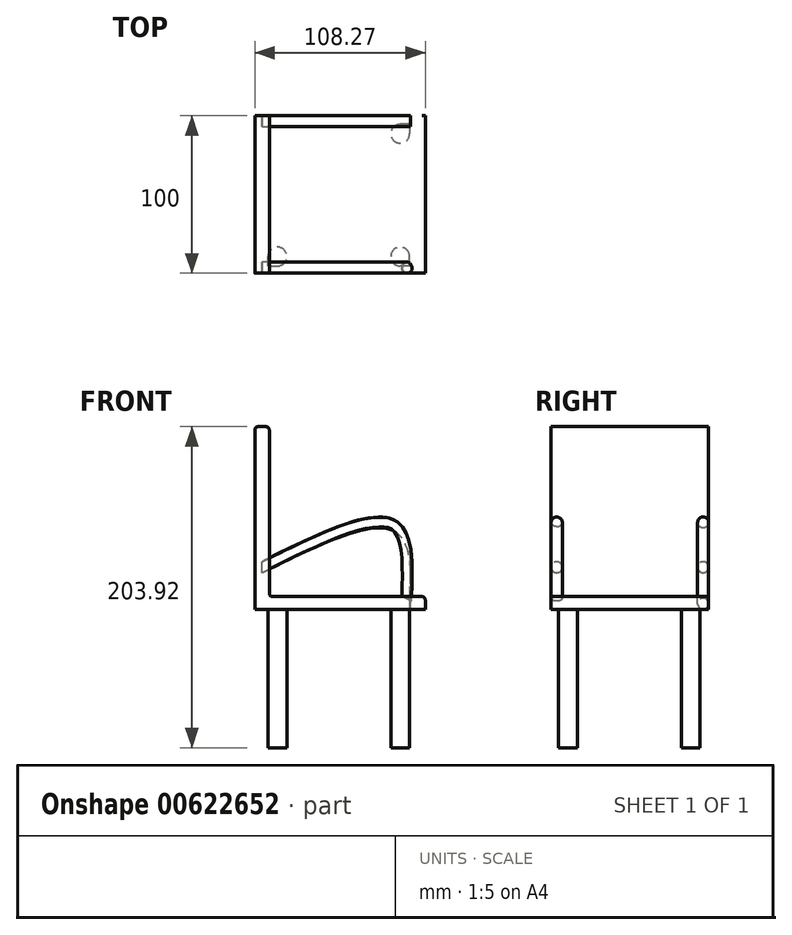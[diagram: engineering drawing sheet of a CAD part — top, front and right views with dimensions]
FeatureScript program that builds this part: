
annotation { "Feature Type Name" : "Feature", "Feature Type Description" : "" }
export const myFeature = defineFeature(function(context is Context, id is Id, definition is map)
    precondition{}
    {
        {
            var Q0;
            Q0=qCreatedBy(makeId("Front.planeOp"),FACE);
            var sketch = newSketch(context, id + "F0", { "sketchPlane" : qUnion([Q0])});
            skLineSegment(sketch, "E0.bottom", {"start": v(-52.86, 60.82) * mm, "end": v(-47.66, 60.82) * mm});
            skLineSegment(sketch, "E0.top", {"start": v(-54.86, -55.1) * mm, "end": v(-45.66, -55.1) * mm});
            skLineSegment(sketch, "E0.left", {"start": v(-54.86, 58.82) * mm, "end": v(-54.86, -55.1) * mm});
            skLineSegment(sketch, "E0.right", {"start": v(-45.66, 58.82) * mm, "end": v(-45.66, -45.1) * mm});
            skLineSegment(sketch, "E1.bottom", {"start": v(-43.66, -47.1) * mm, "end": v(51.4, -47.1) * mm});
            skLineSegment(sketch, "E1.top", {"start": v(-54.86, -55.1) * mm, "end": v(53.4, -55.1) * mm});
            skLineSegment(sketch, "E1.left", {"start": v(-54.86, -47.1) * mm, "end": v(-54.86, -55.1) * mm});
            skLineSegment(sketch, "E1.right", {"start": v(53.4, -49.1) * mm, "end": v(53.4, -55.1) * mm});
            skPoint(sketch, "E2.visualSharp", {"position": v(-54.86, 60.82) * mm});
            skArc(sketch, "E2.filletArc", {"start": v(-52.86, 60.82) * mm, "mid": v(-54.27, 60.23) * mm, "end": v(-54.86, 58.82) * mm});
            skPoint(sketch, "E3.visualSharp", {"position": v(-45.66, 60.82) * mm});
            skArc(sketch, "E3.filletArc", {"start": v(-45.66, 58.82) * mm, "mid": v(-46.24, 60.23) * mm, "end": v(-47.66, 60.82) * mm});
            skPoint(sketch, "E4.visualSharp", {"position": v(53.4, -47.1) * mm});
            skArc(sketch, "E4.filletArc", {"start": v(53.4, -49.1) * mm, "mid": v(52.82, -47.7) * mm, "end": v(51.4, -47.1) * mm});
            skPoint(sketch, "E5.visualSharp", {"position": v(-45.66, -47.1) * mm});
            skArc(sketch, "E5.filletArc", {"start": v(-45.66, -45.1) * mm, "mid": v(-45.07, -46.52) * mm, "end": v(-43.66, -47.1) * mm});
            skSolve(sketch);
        }
        {
            var Q0;
            Q0=makeQuery(id+"F0.imprint","IMPRINT",FACE,{"disambiguationData":[TD([[makeQuery(id+"F0.imprint","IMPRINT",EDGE,{"derivedFrom":sQuery(id+"F0.wireOp",EDGE,"E0.bottom")}),-1.0]])]});
            extrude(context, id + "F1", {"entities" : qUnion([Q0]), "depth" : 100 * mm, "offsetDistance" : 25 * mm});
        }
        {
            var Q0;
            Q0=qCreatedBy(makeId("Front.planeOp"),FACE);
            cPlane(context, id + "F2", {"entities" : qUnion([Q0]), "cplaneType" : CPlaneType.OFFSET, "offset" : 100 * mm, "width" : 150 * mm, "height" : 150 * mm});
        }
        {
            var Q0;
            Q0=qCreatedBy(id+"F2.planeOp",FACE);
            var sketch = newSketch(context, id + "F3", { "sketchPlane" : qUnion([Q0])});
            skFitSpline(sketch, "E6", {"points": [v(-50.26, -26.14) * mm, v(34.27, 0) * mm, v(43.63, -49.33) * mm], "startDerivative": vector(184.27, 91.66) * mm, "endDerivative": vector(-5.37, -149.33) * mm});
            skSolve(sketch);
        }
        {
            var Q0;
            Q0=qCreatedBy(makeId("Right.planeOp"),FACE);
            cPlane(context, id + "F4", {"entities" : qUnion([Q0]), "cplaneType" : CPlaneType.OFFSET, "offset" : 45.7 * mm, "oppositeDirection" : true, "width" : 150 * mm, "height" : 150 * mm});
        }
        {
            var Q0;
            Q0=qCreatedBy(id+"F4.planeOp",FACE);
            var sketch = newSketch(context, id + "F5", { "sketchPlane" : qUnion([Q0])});
            skCircle(sketch, "E7", {"center": v(-96.5, -26.17) * mm, "radius": 3.5 * mm});
            skCircle(sketch, "E8", {"center": v(-3.5, -26.17) * mm, "radius": 3.5 * mm});
            skSolve(sketch);
        }
        {
            var Q0;
            Q0=makeQuery(id+"F5.imprint","IMPRINT",FACE,{"disambiguationData":[TD([[makeQuery(id+"F5.imprint","IMPRINT",EDGE,{"derivedFrom":sQuery(id+"F5.wireOp",EDGE,"E8")}),1.0]])]});
            var Q1;
            Q1=sQuery(id+"F5.wireOp",EDGE,"E7");
            var Q2;
            Q2=sQuery(id+"F3.wireOp",EDGE,"E6");
            sweep(context, id + "F6", {"profiles" : qUnion([Q0]), "surfaceProfiles" : qUnion([Q1]), "path" : qUnion([Q2]), "keepProfileOrientation" : true});
        }
        {
            var Q0;
            Q0=makeQuery(id+"F5.imprint","IMPRINT",FACE,{"disambiguationData":[TD([[makeQuery(id+"F5.imprint","IMPRINT",EDGE,{"derivedFrom":sQuery(id+"F5.wireOp",EDGE,"E7")}),1.0]])]});
            var Q1;
            Q1=sQuery(id+"F3.wireOp",EDGE,"E6");
            sweep(context, id + "F7", {"profiles" : qUnion([Q0]), "path" : qUnion([Q1])});
        }
        {
            var Q0;
            Q0=makeQuery(id+"F1.opExtrude","SWEPT_FACE",FACE,{"disambiguationData":[OSD([sQuery(id+"F0.wireOp",EDGE,"E1.top")])]});
            var sketch = newSketch(context, id + "F8", { "sketchPlane" : qUnion([Q0])});
            skLineSegment(sketch, "E9.bottom", {"start": v(-46.47, 5.43) * mm, "end": v(-40.47, 5.43) * mm});
            skLineSegment(sketch, "E9.right", {"start": v(43.53, 5.43) * mm, "end": v(43.53, 11.43) * mm});
            skPoint(sketch, "E9.middle", {"position": v(-1.47, 50.43) * mm});
            skLineSegment(sketch, "E10.bottom", {"start": v(43.53, 5.43) * mm, "end": v(37.53, 5.43) * mm});
            skLineSegment(sketch, "E11.left", {"start": v(-46.47, 5.43) * mm, "end": v(-46.47, 11.43) * mm});
            skArc(sketch, "E12", {"start": v(37.53, 95.43) * mm, "mid": v(33.28, 85.19) * mm, "end": v(43.53, 89.43) * mm});
            skArc(sketch, "E13", {"start": v(43.53, 11.43) * mm, "mid": v(33.28, 15.67) * mm, "end": v(37.53, 5.43) * mm});
            skArc(sketch, "E14", {"start": v(-46.47, 89.43) * mm, "mid": v(-36.23, 85.19) * mm, "end": v(-40.47, 95.43) * mm});
            skArc(sketch, "E15", {"start": v(-40.47, 5.43) * mm, "mid": v(-36.23, 15.67) * mm, "end": v(-46.47, 11.43) * mm});
            skPoint(sketch, "E16.bottom.start.orphan", {"position": v(43.53, 95.43) * mm});
            skPoint(sketch, "E17.left.start.orphan", {"position": v(-46.47, 95.43) * mm});
            skLineSegment(sketch, "E18", {"start": v(43.53, 95.43) * mm, "end": v(43.53, 89.43) * mm});
            skLineSegment(sketch, "E19", {"start": v(43.53, 95.43) * mm, "end": v(37.53, 95.43) * mm});
            skLineSegment(sketch, "E20", {"start": v(-46.47, 95.43) * mm, "end": v(-46.47, 89.43) * mm});
            skLineSegment(sketch, "E21", {"start": v(-46.47, 95.43) * mm, "end": v(-40.47, 95.43) * mm});
            skSolve(sketch);
        }
        {
            var Q0;
            Q0=makeQuery(id+"F8.imprint","IMPRINT",FACE,{"disambiguationData":[TD([[makeQuery(id+"F8.imprint","IMPRINT",EDGE,{"derivedFrom":sQuery(id+"F8.wireOp",EDGE,"E10.bottom")}),-1.0]])]});
            var Q1;
            Q1=makeQuery(id+"F8.imprint","IMPRINT",FACE,{"disambiguationData":[TD([[makeQuery(id+"F8.imprint","IMPRINT",EDGE,{"derivedFrom":sQuery(id+"F8.wireOp",EDGE,"E12")}),1.0]])]});
            var Q2;
            Q2=makeQuery(id+"F8.imprint","IMPRINT",FACE,{"disambiguationData":[TD([[makeQuery(id+"F8.imprint","IMPRINT",EDGE,{"derivedFrom":sQuery(id+"F8.wireOp",EDGE,"E14")}),1.0]])]});
            var Q3;
            Q3=makeQuery(id+"F8.imprint","IMPRINT",FACE,{"disambiguationData":[TD([[makeQuery(id+"F8.imprint","IMPRINT",EDGE,{"derivedFrom":sQuery(id+"F8.wireOp",EDGE,"E9.bottom")}),1.0]])]});
            extrude(context, id + "F9", {"entities" : qUnion([Q0, Q1, Q2, Q3]), "operationType" : NewBodyOperationType.ADD, "depth" : 88 * mm, "offsetDistance" : 25 * mm});
        }
    });
